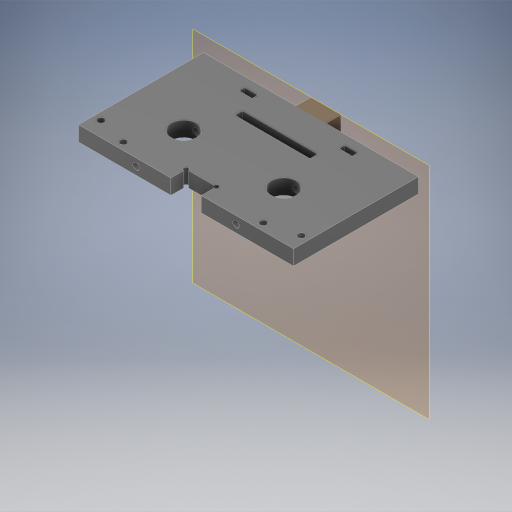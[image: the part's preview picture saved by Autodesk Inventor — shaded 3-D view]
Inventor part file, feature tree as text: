
AUTODESK INVENTOR PART (.ipt)
format: ipt  version: 2024 (Build 280153000, 153)  size: 395,776 bytes
history: native  units: in
note: dims shown in document units (in); Inventor stores cm internally (conversion verified against a paired STEP export)
features: extrude x9, sketch x9, other x4, reference x1, projected_geometry x1
ambient origin geometry x8: Origin, YZ Plane, XZ Plane, XY Plane, X Axis, Y Axis, Z Axis, Center Point
bodies: Body1 (feature_tree)
feature tree (24):
  other  "솔리드1"
  other  "작업 평면1"
  extrude  "돌출1"  Depth=2.9134in
  extrude  "돌출2"  Depth=0.2362in
  extrude  "돌출3"  Depth=1.9685in TaperAngle=0.0deg
  extrude  "돌출5"  Depth=0.4764in
  extrude  "돌출6"  Depth=0.2362in
  extrude  "돌출7"  Depth=0.2402in TaperAngle=0.0deg
  extrude  "돌출9"  Depth=0.4724in
  extrude  "돌출11"  Depth=0.2362in
  extrude  "돌출12"  Depth=0.2362in TaperAngle=0.0deg
  sketch  "스케치1"
  reference  "참조1"
  sketch  "스케치2"
  sketch  "스케치3"
  sketch  "스케치4"
  sketch  "스케치5"
  sketch  "스케치6"
  sketch  "스케치7"
  sketch  "스케치8"
  projected_geometry  "투영된 루프1"
  sketch  "스케치9"
  other  "조립품10"
  other  "body_toptop:1"
